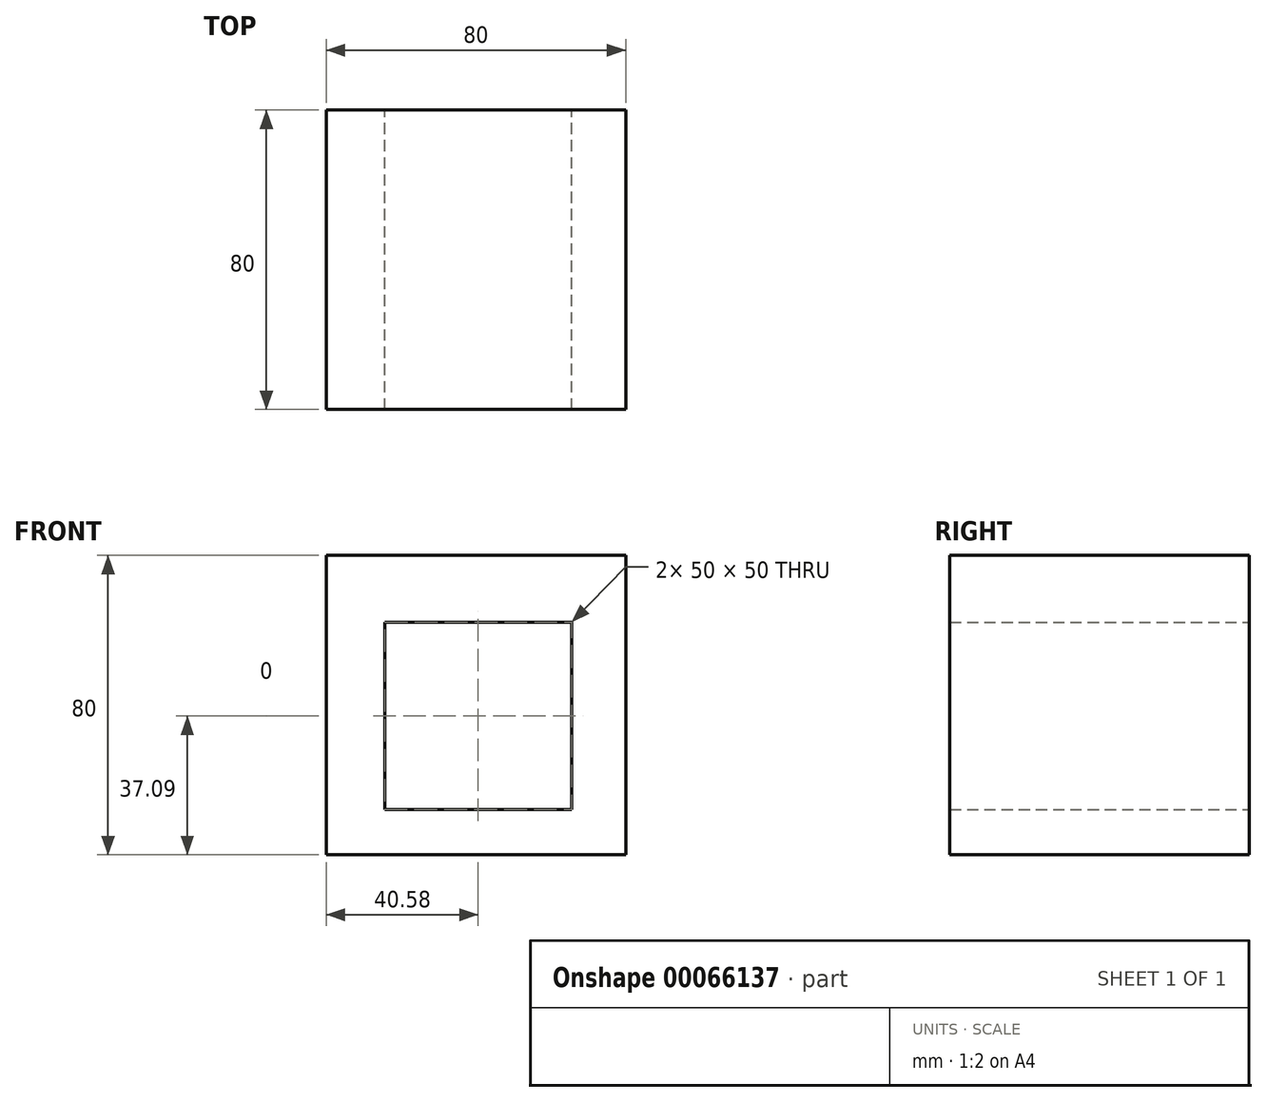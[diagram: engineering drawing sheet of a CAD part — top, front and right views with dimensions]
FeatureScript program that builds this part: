
annotation { "Feature Type Name" : "Feature", "Feature Type Description" : "" }
export const myFeature = defineFeature(function(context is Context, id is Id, definition is map)
    precondition{}
    {
        {
            var Q0;
            Q0=qCreatedBy(makeId("Front.planeOp"),FACE);
            var sketch = newSketch(context, id + "F0", { "sketchPlane" : qUnion([Q0])});
            skLineSegment(sketch, "E0.bottom", {"start": v(0, 0) * mm, "end": v(50, 0) * mm});
            skLineSegment(sketch, "E0.top", {"start": v(0, 50) * mm, "end": v(50, 50) * mm});
            skLineSegment(sketch, "E0.left", {"start": v(0, 0) * mm, "end": v(0, 50) * mm});
            skLineSegment(sketch, "E0.right", {"start": v(50, 0) * mm, "end": v(50, 50) * mm});
            skLineSegment(sketch, "E1.rect.bottom", {"start": v(-15.58, -12.1) * mm, "end": v(64.42, -12.1) * mm});
            skLineSegment(sketch, "E1.rect.top", {"start": v(-15.58, 67.9) * mm, "end": v(64.42, 67.9) * mm});
            skLineSegment(sketch, "E1.rect.left", {"start": v(-15.58, -12.1) * mm, "end": v(-15.58, 67.9) * mm});
            skLineSegment(sketch, "E1.rect.right", {"start": v(64.42, -12.1) * mm, "end": v(64.42, 67.9) * mm});
            skPoint(sketch, "E1.rect.middle", {"position": v(24.42, 27.9) * mm});
            skSolve(sketch);
        }
        {
            var Q0;
            Q0 = qSketchRegion(id + "F0", true);
            extrude(context, id + "F1", {"entities" : qUnion([Q0]), "depth" : 80 * mm});
        }
    });
